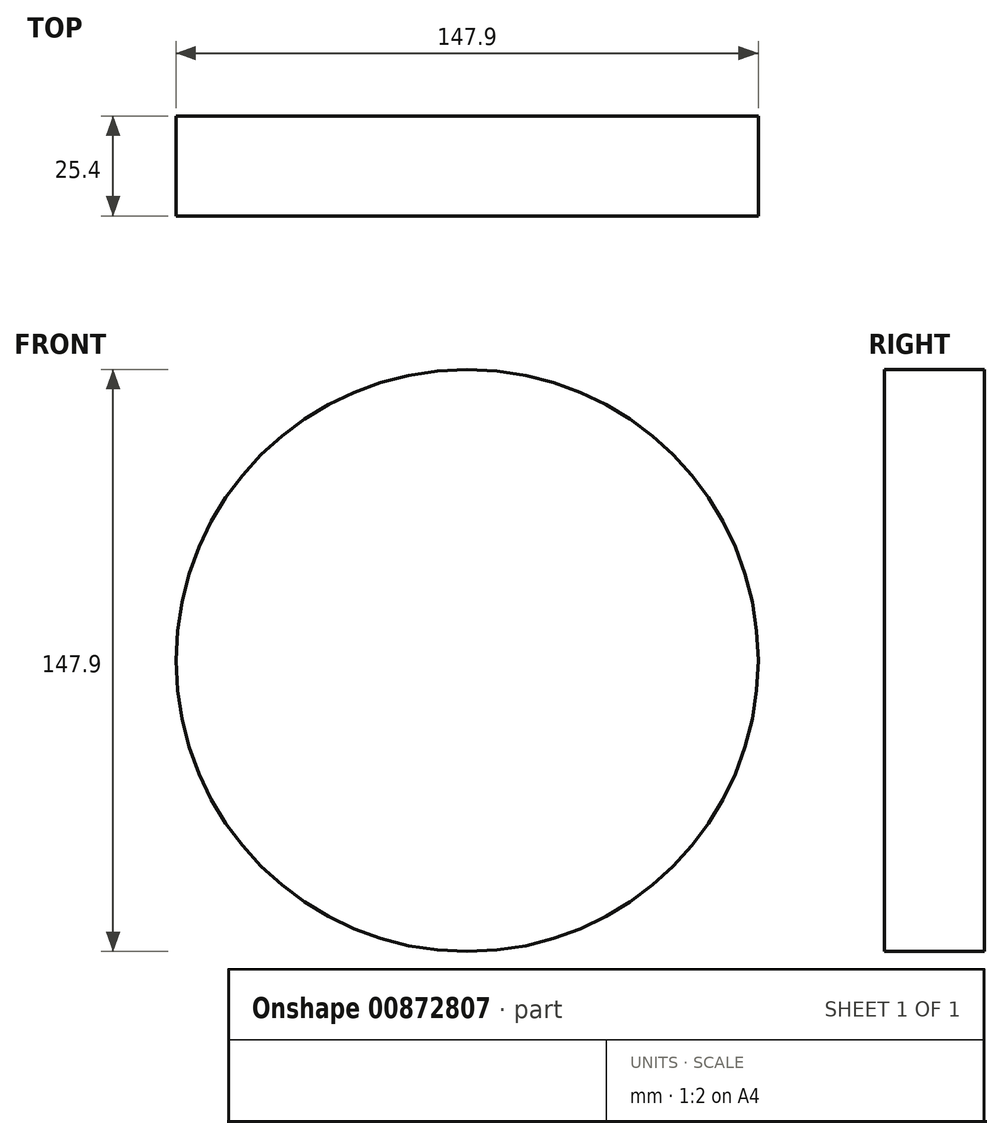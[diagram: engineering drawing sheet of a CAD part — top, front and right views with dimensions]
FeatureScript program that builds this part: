
annotation { "Feature Type Name" : "Feature", "Feature Type Description" : "" }
export const myFeature = defineFeature(function(context is Context, id is Id, definition is map)
    precondition{}
    {
        {
            var Q0;
            Q0=qCreatedBy(makeId("Front.planeOp"),FACE);
            var sketch = newSketch(context, id + "F0", { "sketchPlane" : qUnion([Q0])});
            skCircle(sketch, "E0", {"center": v(-9.05, 0) * mm, "radius": 73.95 * mm});
            skSolve(sketch);
        }
        {
            var Q0;
            Q0 = qSketchRegion(id + "F0", true);
            extrude(context, id + "F1", {"entities" : qUnion([Q0]), "depth" : 25.4 * mm, "offsetDistance" : 25.4 * mm});
        }
    });
